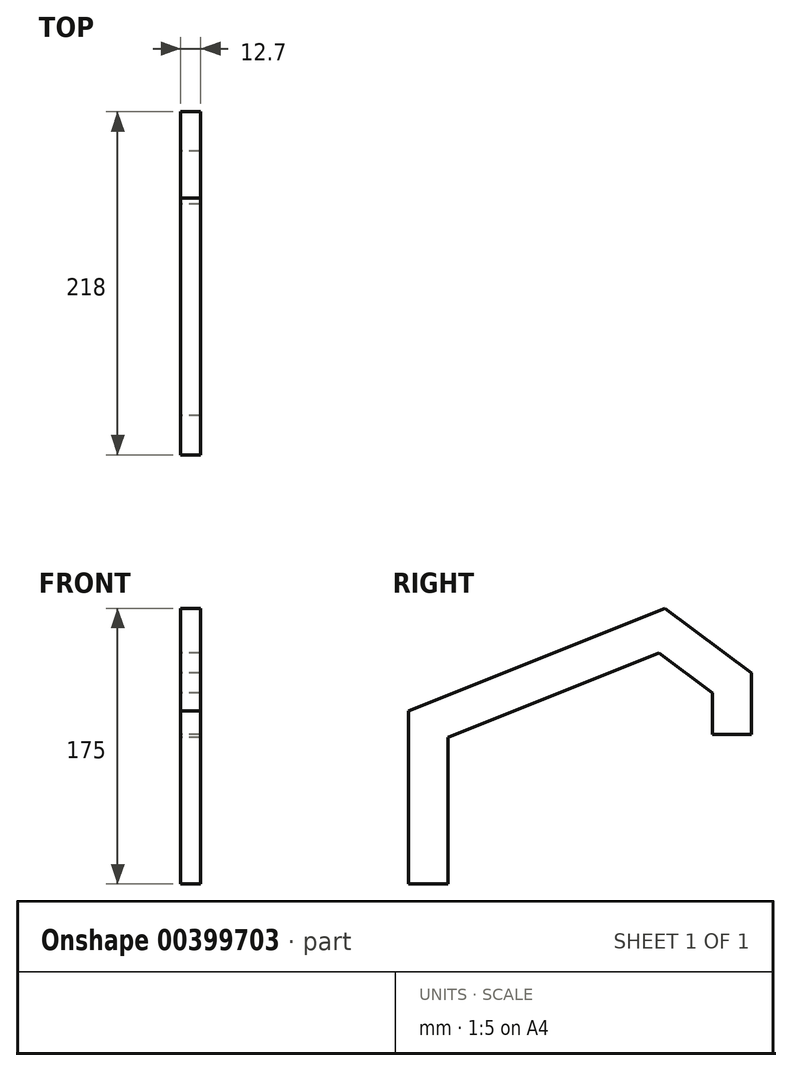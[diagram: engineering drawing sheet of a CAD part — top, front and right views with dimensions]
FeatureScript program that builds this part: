
annotation { "Feature Type Name" : "Feature", "Feature Type Description" : "" }
export const myFeature = defineFeature(function(context is Context, id is Id, definition is map)
    precondition{}
    {
        {
            var Q0;
            Q0=qCreatedBy(makeId("Right.planeOp"),FACE);
            var sketch = newSketch(context, id + "F0", { "sketchPlane" : qUnion([Q0])});
            skLineSegment(sketch, "E0", {"start": v(-159.27, -36.6) * mm, "end": v(-159.27, -146.6) * mm});
            skLineSegment(sketch, "E1", {"start": v(-159.27, -146.6) * mm, "end": v(-134.27, -146.6) * mm});
            skLineSegment(sketch, "E2", {"start": v(-134.27, -146.6) * mm, "end": v(-134.27, -53.54) * mm});
            skLineSegment(sketch, "E3", {"start": v(-134.27, -53.54) * mm, "end": v(0, 0) * mm});
            skLineSegment(sketch, "E4", {"start": v(0, 0) * mm, "end": v(33.73, -25.14) * mm});
            skLineSegment(sketch, "E5", {"start": v(33.73, -25.14) * mm, "end": v(33.73, -51.6) * mm});
            skLineSegment(sketch, "E6", {"start": v(33.73, -51.6) * mm, "end": v(58.73, -51.6) * mm});
            skLineSegment(sketch, "E7", {"start": v(58.73, -51.6) * mm, "end": v(58.73, -12.6) * mm});
            skLineSegment(sketch, "E8", {"start": v(58.73, -12.6) * mm, "end": v(3.73, 28.4) * mm});
            skLineSegment(sketch, "E9", {"start": v(3.73, 28.4) * mm, "end": v(-159.27, -36.6) * mm});
            skLineSegment(sketch, "E10", {"start": v(-159.27, -36.6) * mm, "end": v(-134.27, -53.54) * mm, "construction": true});
            skLineSegment(sketch, "E11", {"start": v(0, 0) * mm, "end": v(3.73, 28.4) * mm, "construction": true});
            skLineSegment(sketch, "E12", {"start": v(33.73, -25.14) * mm, "end": v(58.73, -12.6) * mm, "construction": true});
            skLineSegment(sketch, "E13", {"start": v(-146.77, -146.6) * mm, "end": v(-146.77, -70.9) * mm, "construction": true});
            skLineSegment(sketch, "E14", {"start": v(-122.78, -35.5) * mm, "end": v(-17.93, 6.3) * mm, "construction": true});
            skLineSegment(sketch, "E15", {"start": v(18.95, 1.46) * mm, "end": v(30.9, -7.44) * mm, "construction": true});
            skLineSegment(sketch, "E16", {"start": v(46.23, -38) * mm, "end": v(46.23, -51.6) * mm, "construction": true});
            skPoint(sketch, "E17.visualSharp", {"position": v(-146.77, -45.07) * mm});
            skArc(sketch, "E17.filletArc", {"start": v(-122.78, -35.5) * mm, "mid": v(-140.2, -49.52) * mm, "end": v(-146.77, -70.9) * mm, "construction": true});
            skPoint(sketch, "E18.visualSharp", {"position": v(1.86, 14.2) * mm});
            skArc(sketch, "E18.filletArc", {"start": v(18.95, 1.46) * mm, "mid": v(1.14, 8.7) * mm, "end": v(-17.93, 6.3) * mm, "construction": true});
            skPoint(sketch, "E19.visualSharp", {"position": v(46.23, -18.87) * mm});
            skArc(sketch, "E19.filletArc", {"start": v(46.23, -38) * mm, "mid": v(42.18, -20.9) * mm, "end": v(30.9, -7.44) * mm, "construction": true});
            skSolve(sketch);
        }
        {
            var Q0;
            Q0=makeQuery(id+"F0.imprint","IMPRINT",FACE,{"disambiguationData":[TD([[makeQuery(id+"F0.imprint","IMPRINT",EDGE,{"derivedFrom":sQuery(id+"F0.wireOp",EDGE,"E0")}),1.0]])]});
            extrude(context, id + "F1", {"entities" : qUnion([Q0]), "depth" : 12.7 * mm});
        }
    });
